# Revit family: Domotics-DomesticRanges-GEWISS-SYSTEM_CLIMATE-THERMOSTAT_2M
name_source: partatom
category: Apparecchi elettrici
revit_build: Autodesk Revit 2016 (Build: 20161004_0715(x64)
units: mm (PartAtom-declared; Revit-internal decimal feet)

## family parameters
Condiviso = Sì
Host = Superficie
Mantenere orientamento annotazione = Sì
Numero OmniClass = 23.80.50.11.14
Punto di calcolo locali = Sì
Quota connettore circolare = Usa diametro
Taglio con vuoti quando caricato = Sì
Tipo di parte = Normale
Titolo OmniClass = Switches

## types (2) — shared parameters
Carico apparente = 0 VA
Catalogue = DOMOTICS
Catalogue Range = SYSTEM - DOMESTIC RANGE
Description. = Timed thermostat
Electrocod = 1734
IDF = 44f1a19a-85f3-437f-a63f-dd7429df15ed
IDT = ec2e3b15-b997-49f4-a38e-7a525538048c
Immagine tipo = GW21827.jpg
Larghezza termostato = 46 mm  [stored 0.150919 ft]
N. poli = 2
No. SYSTEM modules = 2
Produttore = GEWISS S.p.A.
Prospetto di default = 1219 mm
SEO = Timed thermostat
Simbolo = SIMBOLO CRONOTERMOSTATO SYSTEM : CRONOTERMOSTATO
Supply voltage = 230 V ac - 50/60 Hz
Technical sheet = https://www.gewiss.com
Temperature adjustment = From +5°C to +40°C
Tipo_ = SYSTEM CRONOTERMOSTATI 2M_BASE : NERO
URL = https://www.gewiss.com
Version file RFA = 19.4
Volt = 230 V
Voltage = 230V ac - 50/60 Hz

## per-type parameters (varying)
| type | Colour | Descrizione | EAN code | Modello |
| GW20827 - White 2M | White | TIMED THERMOSTAT SYSTEM WHITE | 8011564289314 | GW20827 |
| GW21827 - Black 2M | Black | TIMED THERMOSTAT SYSTEM BLACK | 8011564289352 | GW21827 |

note: [stored X ft] marks values corroborated as IEEE doubles in the binary element streams (Revit-internal decimal feet)

## geometry (parser evidence)
native form markers: Sweep x2
no freeform markers — native parametric forms only
